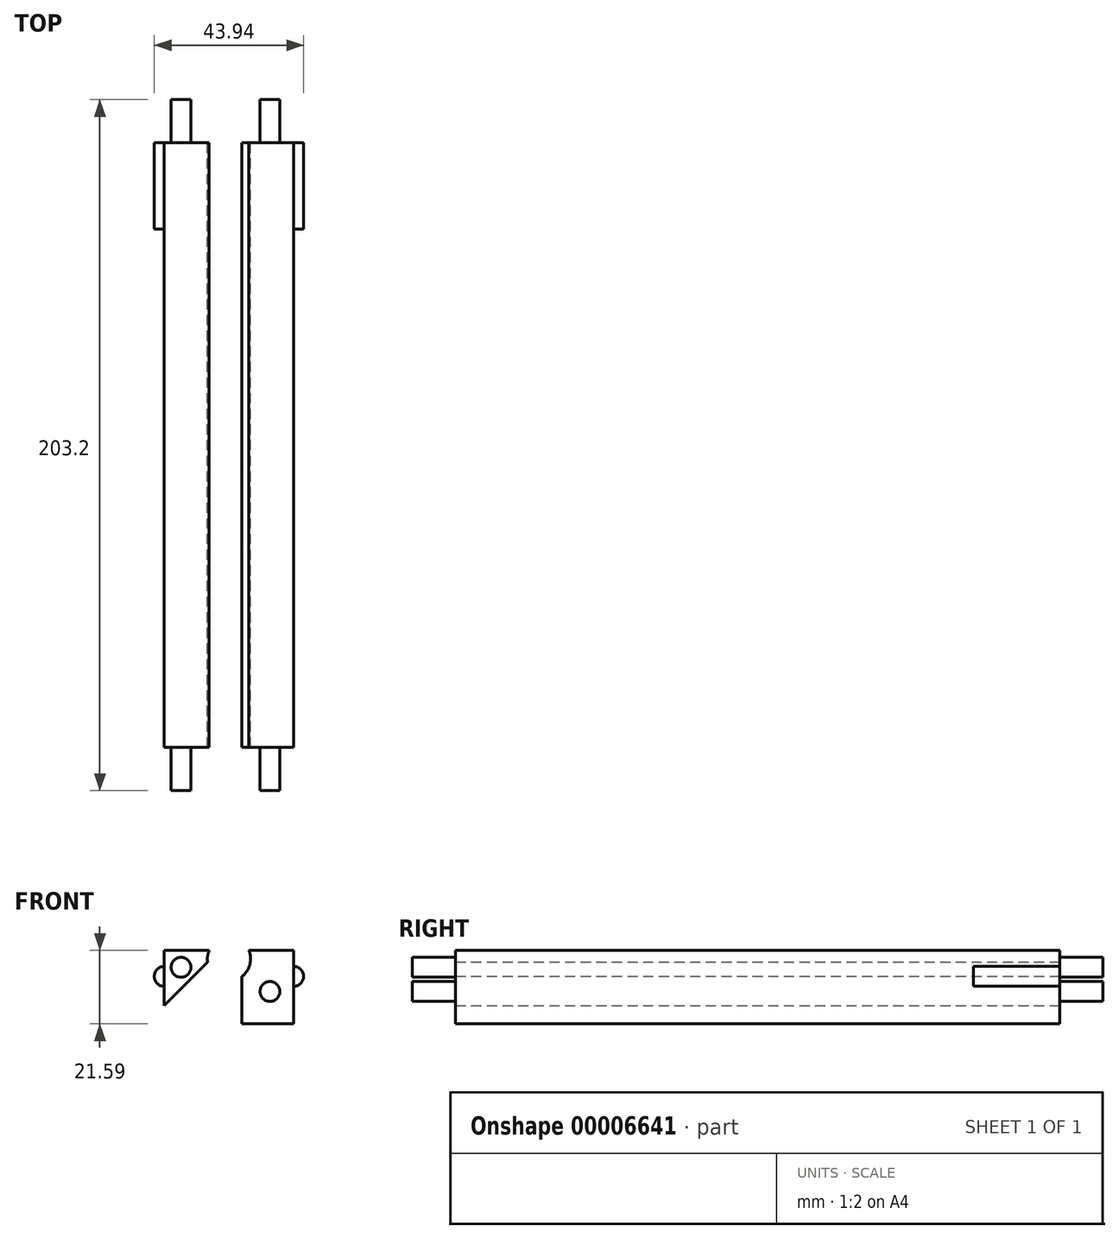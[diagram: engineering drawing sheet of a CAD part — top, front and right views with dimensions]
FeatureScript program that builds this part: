
annotation { "Feature Type Name" : "Feature", "Feature Type Description" : "" }
export const myFeature = defineFeature(function(context is Context, id is Id, definition is map)
    precondition{}
    {
        {
            var Q0;
            Q0=qCreatedBy(makeId("Front.planeOp"),FACE);
            var sketch = newSketch(context, id + "F0", { "sketchPlane" : qUnion([Q0])});
            skLineSegment(sketch, "E0.bottom", {"start": v(-19.05, 19.05) * mm, "end": v(19.05, 19.05) * mm});
            skLineSegment(sketch, "E0.top", {"start": v(-19.05, -19.05) * mm, "end": v(19.05, -19.05) * mm});
            skLineSegment(sketch, "E0.left", {"start": v(-19.05, 19.05) * mm, "end": v(-19.05, -19.05) * mm});
            skLineSegment(sketch, "E0.right", {"start": v(19.05, 19.05) * mm, "end": v(19.05, -19.05) * mm});
            skCircle(sketch, "E1", {"center": v(0, 0) * mm, "radius": 6.35 * mm});
            skLineSegment(sketch, "E2", {"start": v(-19.05, 2.54) * mm, "end": v(19.05, 2.54) * mm});
            skLineSegment(sketch, "E3", {"start": v(-19.05, -19.05) * mm, "end": v(19.05, 19.05) * mm});
            skLineSegment(sketch, "E4", {"start": v(-19.05, -13.66) * mm, "end": v(13.66, 19.05) * mm});
            skLineSegment(sketch, "E5", {"start": v(3.8, 19.05) * mm, "end": v(3.81, -19.05) * mm});
            skSolve(sketch);
        }
        {
            var Q0;
            {var subQ3=sQuery(id+"F0.wireOp",EDGE,"E0.left");var subQ5=sQuery(id+"F0.wireOp",EDGE,"E2");var subQ7=makeQuery(id+"F0.imprint","INTERSECT",VERTEX,{"derivedFrom":[subQ3,subQ5]});Q0=makeQuery(id+"F0.imprint","IMPRINT",FACE,{"disambiguationData":[TD([[makeQuery(id+"F0.imprint","IMPRINT",EDGE,{"disambiguationData":[TD([[subQ7,-1.0]])],"derivedFrom":subQ3}),1.0]])]});}
            var Q1;
            {var subQ3=sQuery(id+"F0.wireOp",EDGE,"E0.top");var subQ7=sQuery(id+"F0.wireOp",EDGE,"E0.right");var subQ9=makeQuery(id+"F0.imprint","INTERSECT",VERTEX,{"derivedFrom":[subQ3,subQ7]});Q1=makeQuery(id+"F0.imprint","IMPRINT",FACE,{"disambiguationData":[TD([[makeQuery(id+"F0.imprint","IMPRINT",EDGE,{"disambiguationData":[TD([[subQ9,1.0]])],"derivedFrom":subQ3}),1.0]])]});}
            extrude(context, id + "F1", {"entities" : qUnion([Q0, Q1]), "depth" : 177.8 * mm});
        }
        {
            var Q0;
            Q0=makeQuery(id+"F1.opExtrude","CAP_FACE",FACE,{"disambiguationData":[OSD([sQuery(id+"F0.wireOp",EDGE,"E0.top"),sQuery(id+"F0.wireOp",EDGE,"E0.right"),sQuery(id+"F0.wireOp",EDGE,"E1"),sQuery(id+"F0.wireOp",EDGE,"E2"),sQuery(id+"F0.wireOp",EDGE,"E5")])],"isStart":false});
            var sketch = newSketch(context, id + "F2", { "sketchPlane" : qUnion([Q0])});
            skCircle(sketch, "E6", {"center": v(12.06, -9.53) * mm, "radius": 2.92 * mm});
            skCircle(sketch, "E7", {"center": v(-14.1, -2.41) * mm, "radius": 2.92 * mm});
            skSolve(sketch);
        }
        {
            var Q0;
            Q0 = qSketchRegion(id + "F2", true);
            extrude(context, id + "F3", {"entities" : qUnion([Q0]), "operationType" : NewBodyOperationType.ADD, "depth" : 12.7 * mm});
        }
        {
            var Q0;
            Q0=qCreatedBy(makeId("Front.planeOp"),FACE);
            var sketch = newSketch(context, id + "F4", { "sketchPlane" : qUnion([Q0])});
            skCircle(sketch, "E8", {"center": v(12.06, -9.53) * mm, "radius": 2.92 * mm});
            skCircle(sketch, "E9", {"center": v(-14.1, -2.41) * mm, "radius": 2.92 * mm});
            skSolve(sketch);
        }
        {
            var Q0;
            Q0=makeQuery(id+"F1.opExtrude","CAP_FACE",FACE,{"disambiguationData":[OSD([sQuery(id+"F0.wireOp",EDGE,"E0.left"),sQuery(id+"F0.wireOp",EDGE,"E1"),sQuery(id+"F0.wireOp",EDGE,"E2"),sQuery(id+"F0.wireOp",EDGE,"E4")])],"isStart":true});
            var sketch = newSketch(context, id + "F5", { "sketchPlane" : qUnion([Q0])});
            skCircle(sketch, "E10", {"center": v(19.05, -5.08) * mm, "radius": 2.92 * mm});
            skSolve(sketch);
        }
        {
            var Q0;
            Q0 = qSketchRegion(id + "F5", true);
            extrude(context, id + "F6", {"entities" : qUnion([Q0]), "operationType" : NewBodyOperationType.ADD, "oppositeDirection" : true, "depth" : 25.4 * mm});
        }
        {
            var Q0;
            Q0=makeQuery(id+"F1.opExtrude","CAP_FACE",FACE,{"disambiguationData":[OSD([sQuery(id+"F0.wireOp",EDGE,"E0.top"),sQuery(id+"F0.wireOp",EDGE,"E0.right"),sQuery(id+"F0.wireOp",EDGE,"E1"),sQuery(id+"F0.wireOp",EDGE,"E2"),sQuery(id+"F0.wireOp",EDGE,"E5")])],"isStart":true});
            var sketch = newSketch(context, id + "F7", { "sketchPlane" : qUnion([Q0])});
            skCircle(sketch, "E11", {"center": v(-19.05, -5.08) * mm, "radius": 2.92 * mm});
            skSolve(sketch);
        }
        {
            var Q0;
            Q0 = qSketchRegion(id + "F7", true);
            extrude(context, id + "F8", {"entities" : qUnion([Q0]), "operationType" : NewBodyOperationType.ADD, "oppositeDirection" : true, "depth" : 25.4 * mm});
        }
        {
            var Q0;
            Q0 = qSketchRegion(id + "F4", true);
            extrude(context, id + "F9", {"entities" : qUnion([Q0]), "operationType" : NewBodyOperationType.ADD, "oppositeDirection" : true, "depth" : 12.7 * mm});
        }
    });
